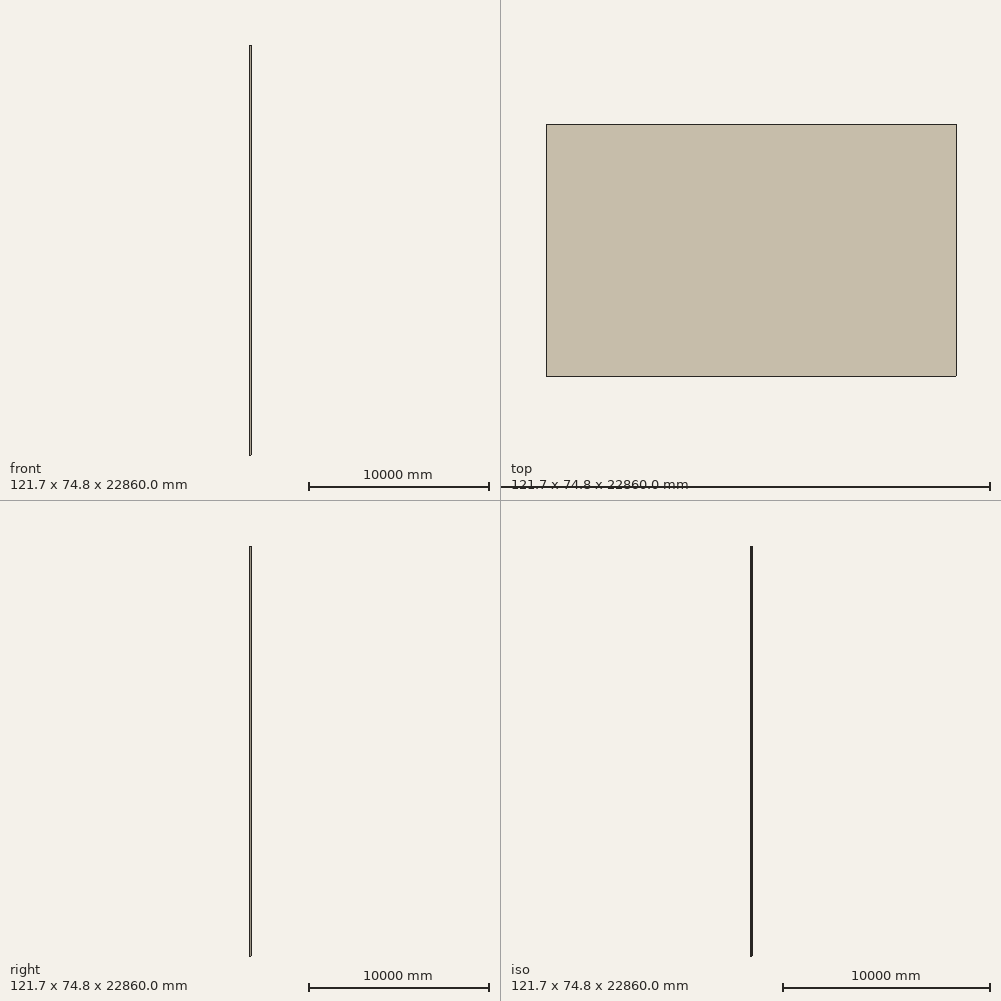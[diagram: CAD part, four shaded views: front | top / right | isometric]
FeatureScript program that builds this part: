
annotation { "Feature Type Name" : "Feature", "Feature Type Description" : "" }
export const myFeature = defineFeature(function(context is Context, id is Id, definition is map)
    precondition{}
    {
        {
            var Q0;
            Q0=qCreatedBy(makeId("Top.planeOp"),FACE);
            var sketch = newSketch(context, id + "F0", { "sketchPlane" : qUnion([Q0])});
            skLineSegment(sketch, "E0.bottom", {"start": v(59.5, 44.63) * mm, "end": v(-62.21, 44.63) * mm});
            skLineSegment(sketch, "E0.top", {"start": v(59.5, -30.15) * mm, "end": v(-62.21, -30.15) * mm});
            skLineSegment(sketch, "E0.left", {"start": v(59.5, 44.63) * mm, "end": v(59.5, -30.15) * mm});
            skLineSegment(sketch, "E0.right", {"start": v(-62.21, 44.63) * mm, "end": v(-62.21, -30.15) * mm});
            skSolve(sketch);
        }
        {
            var Q0;
            Q0=makeQuery(id+"F0.imprint","IMPRINT",FACE,{"disambiguationData":[TD([[makeQuery(id+"F0.imprint","IMPRINT",EDGE,{"derivedFrom":sQuery(id+"F0.wireOp",EDGE,"E0.bottom")}),1.0]])]});
            extrude(context, id + "F1", {"entities" : qUnion([Q0]), "depth" : 22860 * mm, "offsetDistance" : 25.4 * mm});
        }
    });
